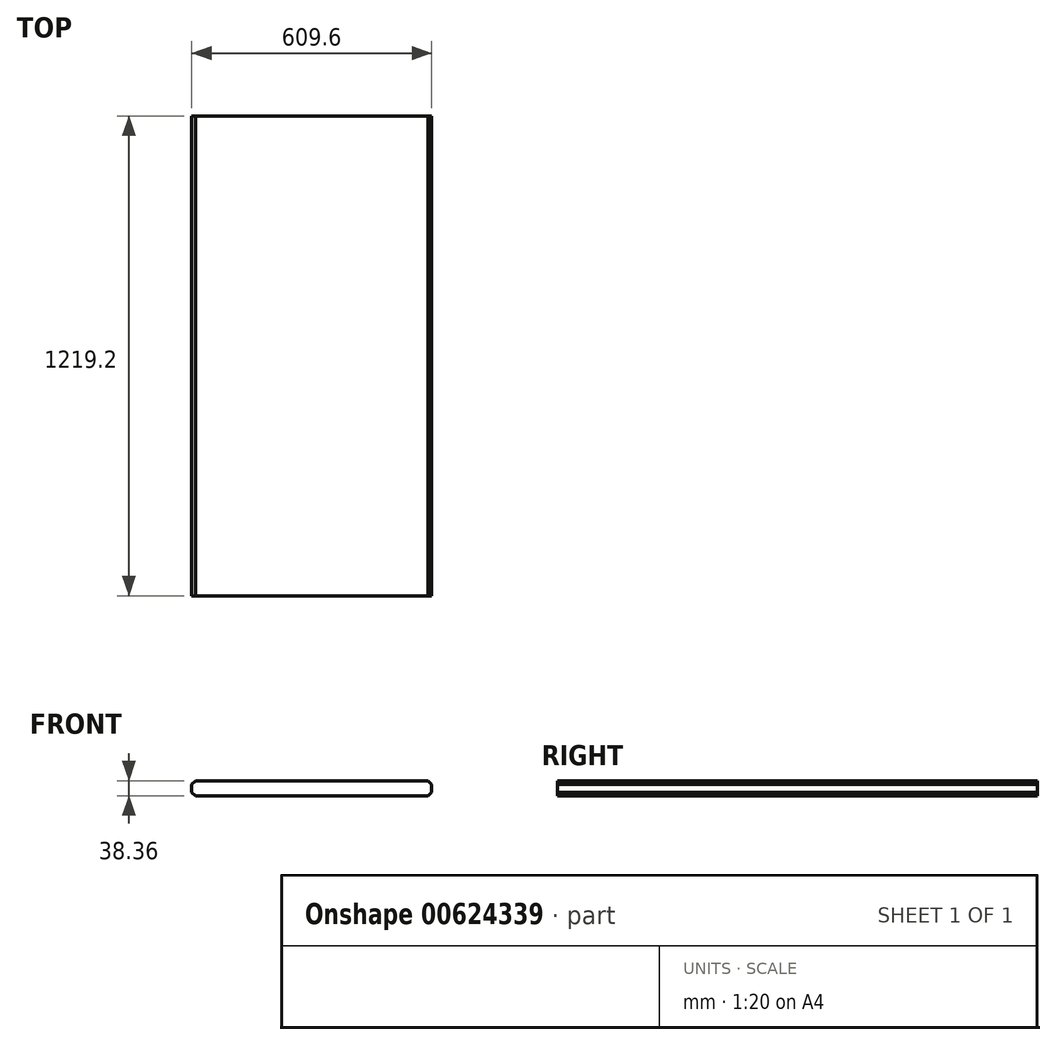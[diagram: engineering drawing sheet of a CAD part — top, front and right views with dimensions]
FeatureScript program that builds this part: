
annotation { "Feature Type Name" : "Feature", "Feature Type Description" : "" }
export const myFeature = defineFeature(function(context is Context, id is Id, definition is map)
    precondition{}
    {
        {
            var Q0;
            Q0=qCreatedBy(makeId("Top.planeOp"),FACE);
            var sketch = newSketch(context, id + "F0", { "sketchPlane" : qUnion([Q0])});
            skLineSegment(sketch, "E0.bottom", {"start": v(-304.8, 609.6) * mm, "end": v(304.8, 609.6) * mm});
            skLineSegment(sketch, "E0.top", {"start": v(-304.8, -609.6) * mm, "end": v(304.8, -609.6) * mm});
            skLineSegment(sketch, "E0.left", {"start": v(-304.8, 609.6) * mm, "end": v(-304.8, -609.6) * mm});
            skLineSegment(sketch, "E0.right", {"start": v(304.8, 609.6) * mm, "end": v(304.8, -609.6) * mm});
            skLineSegment(sketch, "E1", {"start": v(-304.8, 0) * mm, "end": v(304.8, 0) * mm, "construction": true});
            skLineSegment(sketch, "E2", {"start": v(0, 609.6) * mm, "end": v(0, -609.6) * mm, "construction": true});
            skSolve(sketch);
        }
        {
            var Q0;
            Q0=makeQuery(id+"F0.imprint","IMPRINT",FACE,{"disambiguationData":[TD([[makeQuery(id+"F0.imprint","IMPRINT",EDGE,{"derivedFrom":sQuery(id+"F0.wireOp",EDGE,"E0.bottom")}),-1.0]])]});
            extrude(context, id + "F1", {"entities" : qUnion([Q0]), "endBound" : BoundingType.SYMMETRIC, "depth" : 38.35 * mm, "offsetDistance" : 25.4 * mm});
        }
        {
            var Q0;
            Q0=makeQuery(id+"F1.opExtrude","CAP_EDGE",EDGE,{"disambiguationData":[OSD([sQuery(id+"F0.wireOp",EDGE,"E0.left")])],"isStart":false});
            var Q1;
            Q1=makeQuery(id+"F1.opExtrude","CAP_EDGE",EDGE,{"disambiguationData":[OSD([sQuery(id+"F0.wireOp",EDGE,"E0.left")])],"isStart":true});
            var Q2;
            Q2=makeQuery(id+"F1.opExtrude","CAP_EDGE",EDGE,{"disambiguationData":[OSD([sQuery(id+"F0.wireOp",EDGE,"E0.right")])],"isStart":false});
            var Q3;
            Q3=makeQuery(id+"F1.opExtrude","CAP_EDGE",EDGE,{"disambiguationData":[OSD([sQuery(id+"F0.wireOp",EDGE,"E0.right")])],"isStart":true});
            chamfer(context, id + "F2", {"entities" : qUnion([Q0, Q1, Q2, Q3]), "width" : 9.52 * mm, "tangentPropagation" : true});
        }
    });
